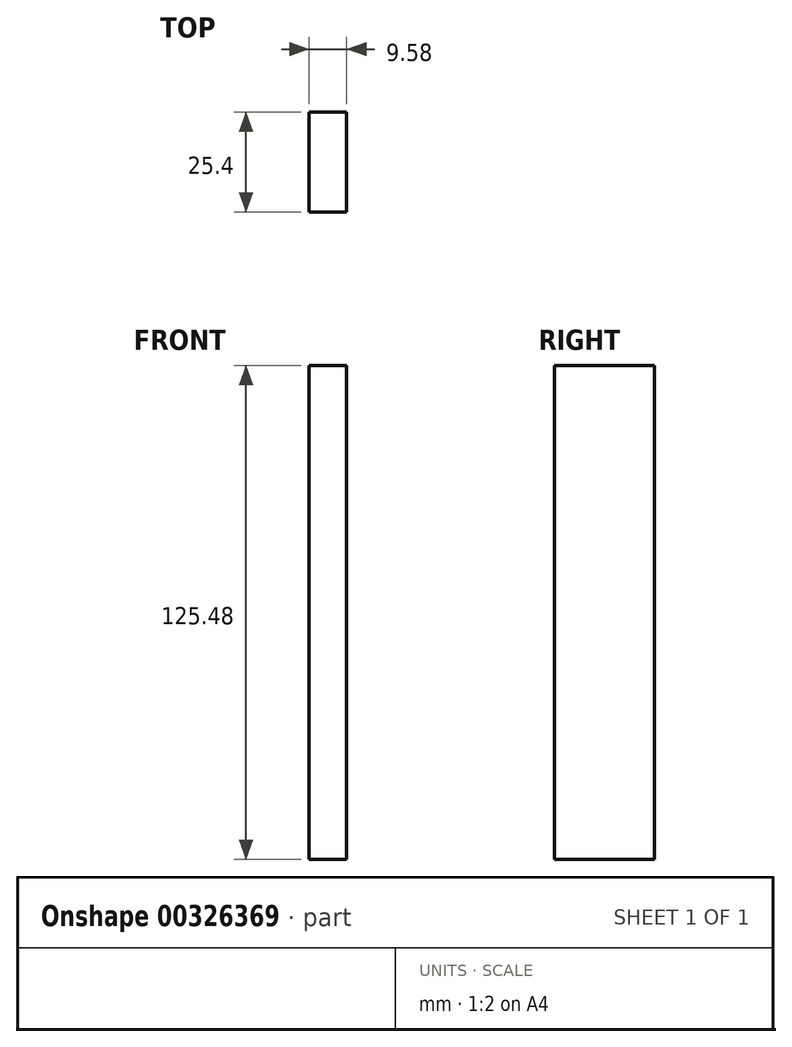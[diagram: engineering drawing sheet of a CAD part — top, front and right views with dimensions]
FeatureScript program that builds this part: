
annotation { "Feature Type Name" : "Feature", "Feature Type Description" : "" }
export const myFeature = defineFeature(function(context is Context, id is Id, definition is map)
    precondition{}
    {
        {
            var Q0;
            Q0=qCreatedBy(makeId("Front.planeOp"),FACE);
            var sketch = newSketch(context, id + "F0", { "sketchPlane" : qUnion([Q0])});
            skLineSegment(sketch, "E0.bottom", {"start": v(-123.45, 50.03) * mm, "end": v(-113.87, 50.03) * mm});
            skLineSegment(sketch, "E0.top", {"start": v(-123.45, -75.45) * mm, "end": v(-113.87, -75.45) * mm});
            skLineSegment(sketch, "E0.left", {"start": v(-123.45, 50.03) * mm, "end": v(-123.45, -75.45) * mm});
            skLineSegment(sketch, "E0.right", {"start": v(-113.87, 50.03) * mm, "end": v(-113.87, -75.45) * mm});
            skSolve(sketch);
        }
        {
            var Q0;
            Q0 = qSketchRegion(id + "F0", true);
            extrude(context, id + "F1", {"entities" : qUnion([Q0]), "depth" : 25.4 * mm});
        }
    });
